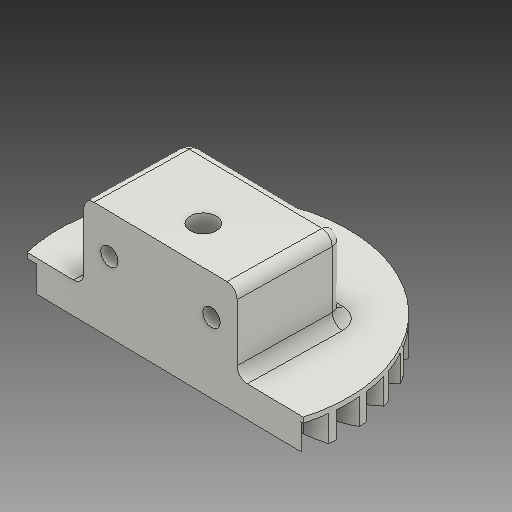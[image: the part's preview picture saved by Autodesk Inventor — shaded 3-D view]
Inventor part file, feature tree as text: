
AUTODESK INVENTOR PART (.ipt)
format: ipt  version: 2018 (Build 220112000, 112)  size: 331,776 bytes
history: native  units: mm
features: other x13, sketch x9, plane x4
ambient origin geometry x8: Origin, YZ Plane, XZ Plane, XY Plane, X Axis, Y Axis, Z Axis, Center Point
bodies: Volumenkörper1 (feature_tree)
feature tree (26):
  other  "Stirnzahnrad11_MIR.ipt"
  other  "Volumenkörper1::Stirnzahnrad11_MIR.ipt"
  other  "Bezeichnung1"
  sketch  "Sketch1"  dims[d0=10.0mm]
  sketch  "Sketch2"  dims[d16=40.0mm d17=0.0mm d41=0.0mm d43=40.0mm d46=40.0mm d47=0.0mm d48=0.0mm]
  sketch  "Skizze9"
  sketch  "Skizze10"
  sketch  "Skizze11"
  sketch  "Skizze12"
  sketch  "Skizze13"
  sketch  "Skizze14"
  sketch  "Skizze15"
  plane  "XZ Plane_1"
  plane  "Work Plane2"
  plane  "Work Plane8"
  plane  "Work Plane9"
  other  "Z Axis_1"
  other  "Flä1"
  other  "Flä1::Abgeleitet"
  other  "Abstands-iMate"
  other  "Ausrichtungs-iMate"
  other  "Netz-iMate"
  other  "Achsen-iMate"
  other  "Positions-iMate"
  other  "Netz-iMate 2"
  other  "Startebenen-iMate"
